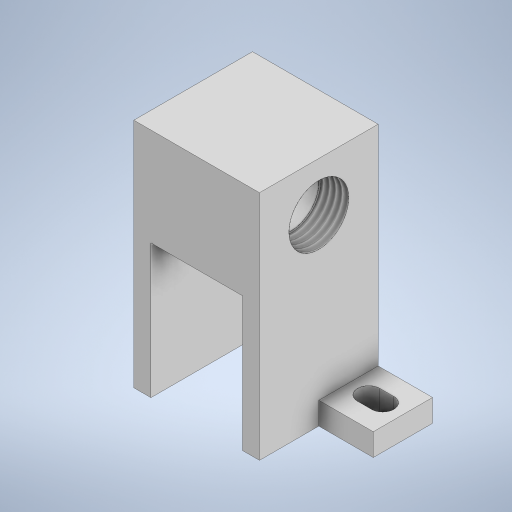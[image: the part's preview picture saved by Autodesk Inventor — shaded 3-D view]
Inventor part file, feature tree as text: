
AUTODESK INVENTOR PART (.ipt)
format: ipt  version: 2024.2 (Build 282272000, 272)  size: 301,056 bytes
history: native  units: in
note: dims shown in document units (in); Inventor stores cm internally (conversion verified against a paired STEP export)
features: sketch x7, extrude x5, hole x2
ambient origin geometry x8: Origin, YZ Plane, XZ Plane, XY Plane, X Axis, Y Axis, Z Axis, Center Point
bodies: Solid1 (feature_tree)
feature tree (14):
  extrude  "Extrusion1"  Depth=0.6693in
  extrude  "Extrusion2"  Depth=0.5157in
  extrude  "Extrusion3"  Depth=0.3071in
  extrude  "Extrusion4"  Depth=0.126in TaperAngle=0.0deg
  extrude  "Extrusion5"  Depth=0.126in
  hole  "Hole2"  [1 undecoded]
  hole  "Hole3"  [1 undecoded]
  sketch  "Sketch1"  dims[d0=0.7087in d1=0.6693in]
  sketch  "Sketch2"  dims[d2=1.3071in d3=0.0in d4=0.5157in]
  sketch  "Sketch4"  dims[d5=0.7559in d6=0.0in d7=0.3071in]
  sketch  "Sketch5"  dims[d8=0.3071in d9=0.126in d10=0.0in]
  sketch  "Sketch6"  dims[d11=0.1142in d12=0.126in]
  sketch  "Sketch8"  dims[d13=0.0787in d14=0.126in]
  sketch  "Sketch9"  dims[d15=0.0in d16=0.0in d17=0.1142in d18=0.0787in d19=0.126in d20=0.126in d21=0.2756in d22=0.315in d23=0.0in d24=0.0in d33=0.2756in d34=0.3372in d35=0.1575in d36=0.1575in d37=0.0787in d38=90.0deg d39=0.1575in d40=0.0in d41=0.2756in d42=0.3372in d43=0.1575in d44=0.1575in d45=0.0787in d46=90.0deg d47=0.1575in d48=0.0in]
note: 2 required parameter values undecoded (feature->parameter linkage not recoverable at this tier; creation-order binding heuristic only, values carry confidence <= 0.55)
